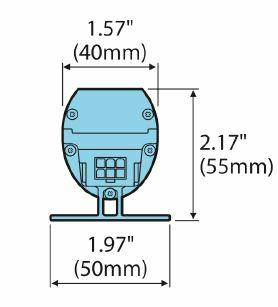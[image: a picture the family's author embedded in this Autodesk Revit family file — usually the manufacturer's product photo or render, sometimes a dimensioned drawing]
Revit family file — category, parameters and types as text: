
# Revit family: Lighting-Linear-Acclaim-Adapt-Linear-DMX
name_source: partatom
category: Lighting Fixtures
units: mm (PartAtom-declared; Revit-internal decimal feet)

## family parameters
Cut with Voids When Loaded = No
Host = Face
Light Source = Yes
Part Type = Normal
Room Calculation Point = No
Round Connector Dimension = Use Diameter
Shared = No

## types (1)
- Lighting-Linear-Acclaim-Adapt-Linear-DMX
    Apparent Load = 0 VA
    Color Filter = 16777215
    Default Elevation = 48 "
    Description = Linear LED
    Dimming Lamp Color Temperature Shift = <None>
    Emit from Line Length = 24 "
    Height = 2.17 "
    Housing Finish = Aluminum
    Lamp = LED
    Length = 24 "
    Manufacturer = Acclaim Lighting
    Model = Adapt Linear DMX
    Number of Poles = 1
    Photometric Web File = Load File
    Power Factor = 1
    Tilt Angle = -90.00°
    URL = http://www.acclaimlighting.com
    Voltage = 0 V
    Width = 1.97 "

## geometry (parser evidence)
native form markers: Blend x13, Sweep x2
no freeform markers — native parametric forms only
